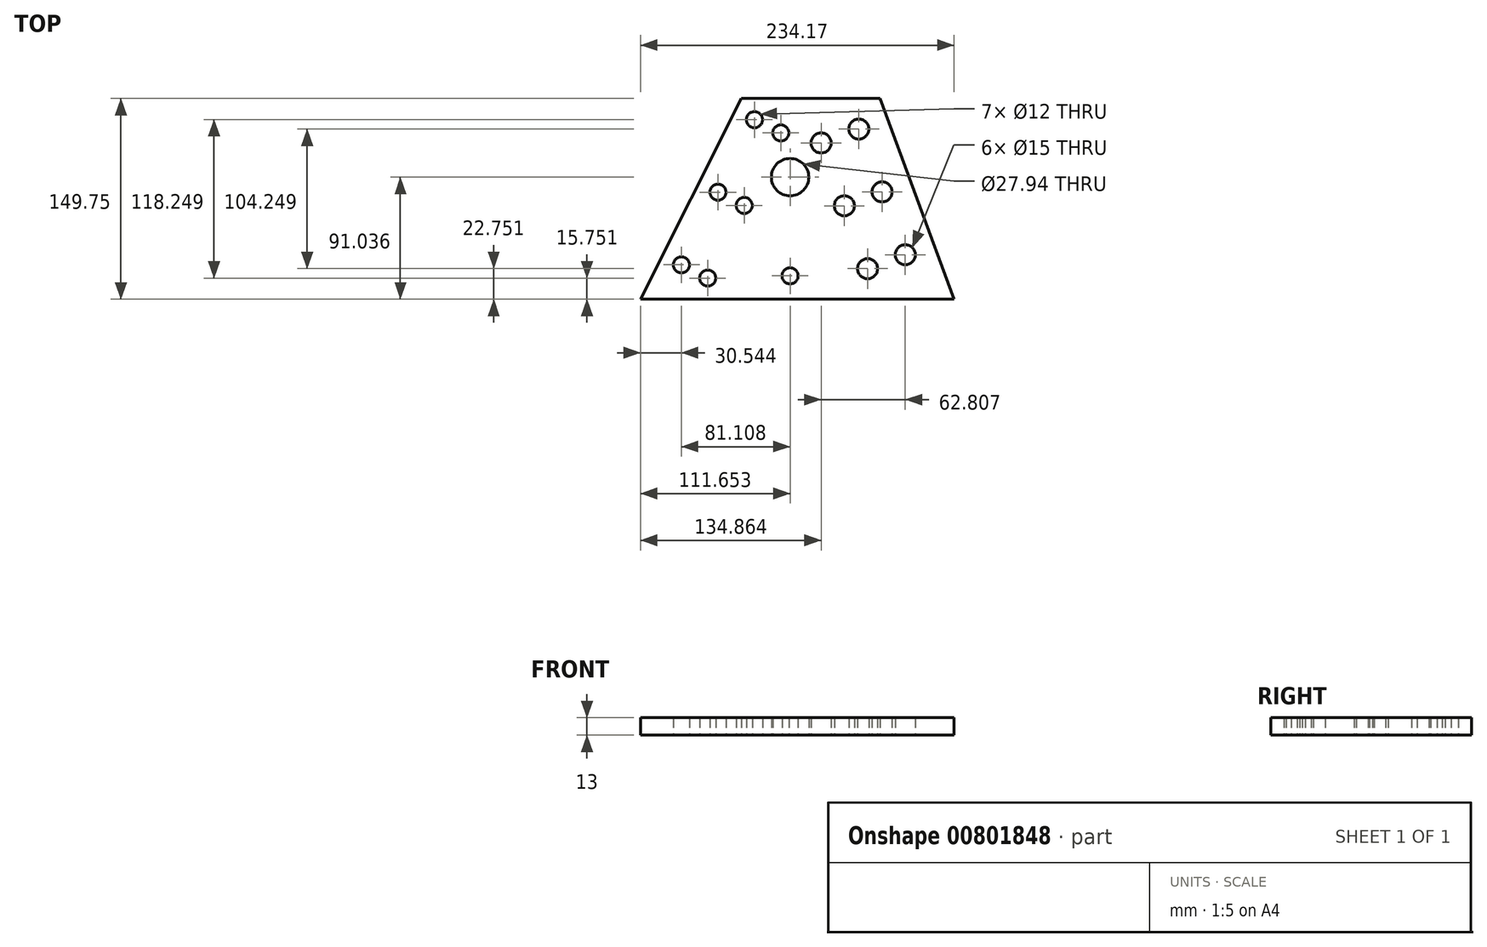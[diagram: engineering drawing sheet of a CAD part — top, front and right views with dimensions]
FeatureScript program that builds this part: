
annotation { "Feature Type Name" : "Feature", "Feature Type Description" : "" }
export const myFeature = defineFeature(function(context is Context, id is Id, definition is map)
    precondition{}
    {
        {
            var Q0;
            Q0=qCreatedBy(makeId("Top.planeOp"),FACE);
            var sketch = newSketch(context, id + "F0", { "sketchPlane" : qUnion([Q0])});
            skLineSegment(sketch, "E0", {"start": v(0, 0) * mm, "end": v(-107.38, -213.25) * mm, "construction": true});
            skLineSegment(sketch, "E1", {"start": v(-107.38, -213.25) * mm, "end": v(78.76, -213.25) * mm, "construction": true});
            skLineSegment(sketch, "E2", {"start": v(78.76, -213.25) * mm, "end": v(0, 0) * mm, "construction": true});
            skLineSegment(sketch, "E3", {"start": v(-124.54, -187.85) * mm, "end": v(109.63, -187.85) * mm});
            skLineSegment(sketch, "E4", {"start": v(-49.14, -38.1) * mm, "end": v(54.32, -38.1) * mm});
            skLineSegment(sketch, "E5", {"start": v(-49.14, -38.1) * mm, "end": v(-124.54, -187.85) * mm});
            skLineSegment(sketch, "E6", {"start": v(54.32, -38.1) * mm, "end": v(109.63, -187.85) * mm});
            skLineSegment(sketch, "E7", {"start": v(-19.78, -63.74) * mm, "end": v(-74.35, -172.1) * mm, "construction": true});
            skLineSegment(sketch, "E8", {"start": v(-94, -162.2) * mm, "end": v(-39.43, -53.85) * mm, "construction": true});
            skLineSegment(sketch, "E9", {"start": v(-19.78, -63.74) * mm, "end": v(-29.6, -58.8) * mm, "construction": true});
            skLineSegment(sketch, "E10", {"start": v(-39.43, -53.85) * mm, "end": v(-29.6, -58.8) * mm, "construction": true});
            skLineSegment(sketch, "E11", {"start": v(-74.35, -172.1) * mm, "end": v(-94, -162.2) * mm, "construction": true});
            skPoint(sketch, "E12", {"position": v(-66.71, -108.03) * mm});
            skPoint(sketch, "E13", {"position": v(-47.06, -117.92) * mm});
            skCircle(sketch, "E14", {"center": v(-39.43, -53.85) * mm, "radius": 2.25 * mm});
            skCircle(sketch, "E15", {"center": v(-19.78, -63.74) * mm, "radius": 2.25 * mm});
            skCircle(sketch, "E16", {"center": v(-47.06, -117.92) * mm, "radius": 2.25 * mm});
            skCircle(sketch, "E17", {"center": v(-66.71, -108.03) * mm, "radius": 2.25 * mm});
            skCircle(sketch, "E18", {"center": v(-94, -162.2) * mm, "radius": 2.25 * mm});
            skCircle(sketch, "E19", {"center": v(-74.35, -172.1) * mm, "radius": 2.25 * mm});
            skLineSegment(sketch, "E20", {"start": v(10.32, -71.24) * mm, "end": v(44.99, -165.1) * mm, "construction": true});
            skLineSegment(sketch, "E21", {"start": v(44.99, -165.1) * mm, "end": v(73.13, -154.7) * mm, "construction": true});
            skLineSegment(sketch, "E22", {"start": v(73.13, -154.7) * mm, "end": v(38.47, -60.85) * mm, "construction": true});
            skPoint(sketch, "E23", {"position": v(59.06, -159.9) * mm});
            skLineSegment(sketch, "E24", {"start": v(38.47, -60.85) * mm, "end": v(10.32, -71.24) * mm, "construction": true});
            skPoint(sketch, "E25", {"position": v(27.66, -118.17) * mm});
            skPoint(sketch, "E26", {"position": v(55.8, -107.78) * mm});
            skCircle(sketch, "E27", {"center": v(10.32, -71.24) * mm, "radius": 3.25 * mm});
            skCircle(sketch, "E28", {"center": v(27.66, -118.17) * mm, "radius": 3.25 * mm});
            skCircle(sketch, "E29", {"center": v(44.99, -165.1) * mm, "radius": 3.25 * mm});
            skCircle(sketch, "E30", {"center": v(73.13, -154.7) * mm, "radius": 3.25 * mm});
            skCircle(sketch, "E31", {"center": v(55.8, -107.78) * mm, "radius": 3.25 * mm});
            skCircle(sketch, "E32", {"center": v(38.47, -60.85) * mm, "radius": 3.25 * mm});
            skLineSegment(sketch, "E33.0", {"start": v(-40.53, -47.14) * mm, "end": v(-13.74, -60.63) * mm, "construction": true});
            skLineSegment(sketch, "E34.0", {"start": v(-40.53, -47.14) * mm, "end": v(-45.48, -56.96) * mm, "construction": true});
            skLineSegment(sketch, "E35.0", {"start": v(-13.74, -60.63) * mm, "end": v(-18.68, -70.46) * mm, "construction": true});
            skLineSegment(sketch, "E36.0", {"start": v(-45.48, -56.96) * mm, "end": v(-18.68, -70.46) * mm, "construction": true});
            skLineSegment(sketch, "E37.0", {"start": v(40.56, -52.08) * mm, "end": v(3.04, -65.94) * mm, "construction": true});
            skLineSegment(sketch, "E38.0", {"start": v(45.75, -66.15) * mm, "end": v(8.23, -80.01) * mm, "construction": true});
            skLineSegment(sketch, "E39.0", {"start": v(45.75, -66.15) * mm, "end": v(40.56, -52.08) * mm, "construction": true});
            skLineSegment(sketch, "E40.0", {"start": v(8.23, -80.01) * mm, "end": v(3.04, -65.94) * mm, "construction": true});
            skCircle(sketch, "E41", {"center": v(-12.89, -96.81) * mm, "radius": 13.34 * mm});
            skCircle(sketch, "E42", {"center": v(-12.89, -96.81) * mm, "radius": 26.99 * mm, "construction": true});
            skCircle(sketch, "E43", {"center": v(-12.89, -96.81) * mm, "radius": 102.23 * mm, "construction": true});
            skCircle(sketch, "E44", {"center": v(-12.89, -170.41) * mm, "radius": 3.24 * mm});
            skPoint(sketch, "E45", {"position": v(-12.89, -167.17) * mm});
            skPoint(sketch, "E46", {"position": v(-12.89, -173.65) * mm});
            skSolve(sketch);
        }
        {
            var Q0;
            Q0=qCreatedBy(makeId("Top.planeOp"),FACE);
            var sketch = newSketch(context, id + "F1", { "sketchPlane" : qUnion([Q0])});
            skPoint(sketch, "E47.0", {"position": v(-12.89, -96.81) * mm});
            skPoint(sketch, "E48.0", {"position": v(-12.89, -170.41) * mm});
            skCircle(sketch, "E49.0", {"center": v(-12.89, -96.81) * mm, "radius": 13.34 * mm});
            skCircle(sketch, "E50.0", {"center": v(-12.89, -170.41) * mm, "radius": 3.24 * mm});
            skLineSegment(sketch, "E51", {"start": v(12.51, -96.81) * mm, "end": v(12.51, -170.41) * mm});
            skLineSegment(sketch, "E52", {"start": v(-38.29, -96.81) * mm, "end": v(-38.29, -170.41) * mm});
            skArc(sketch, "E53", {"start": v(12.51, -96.81) * mm, "mid": v(-12.89, -71.41) * mm, "end": v(-38.29, -96.81) * mm});
            skArc(sketch, "E54", {"start": v(-38.29, -170.41) * mm, "mid": v(-12.89, -195.81) * mm, "end": v(12.51, -170.41) * mm});
            skSolve(sketch);
        }
        {
            var Q0;
            Q0=qCreatedBy(makeId("Top.planeOp"),FACE);
            var sketch = newSketch(context, id + "F2", { "sketchPlane" : qUnion([Q0])});
            skPoint(sketch, "E55.0", {"position": v(-49.14, -38.1) * mm});
            skPoint(sketch, "E56.0", {"position": v(54.32, -38.1) * mm});
            skPoint(sketch, "E57.0", {"position": v(109.63, -187.85) * mm});
            skPoint(sketch, "E58.0", {"position": v(-124.54, -187.85) * mm});
            skPoint(sketch, "E59.0", {"position": v(-94, -162.2) * mm});
            skPoint(sketch, "E60.0", {"position": v(-74.35, -172.1) * mm});
            skPoint(sketch, "E61.0", {"position": v(-47.06, -117.92) * mm});
            skPoint(sketch, "E62.0", {"position": v(-66.71, -108.03) * mm});
            skPoint(sketch, "E63.0", {"position": v(-39.43, -53.85) * mm});
            skPoint(sketch, "E64.0", {"position": v(-19.78, -63.74) * mm});
            skPoint(sketch, "E65.0", {"position": v(10.32, -71.24) * mm});
            skPoint(sketch, "E66.0", {"position": v(27.66, -118.17) * mm});
            skPoint(sketch, "E67.0", {"position": v(44.99, -165.1) * mm});
            skPoint(sketch, "E68.0", {"position": v(73.13, -154.7) * mm});
            skPoint(sketch, "E69.0", {"position": v(55.8, -107.78) * mm});
            skPoint(sketch, "E70.0", {"position": v(38.47, -60.85) * mm});
            skPoint(sketch, "E71.0", {"position": v(-12.89, -96.81) * mm});
            skPoint(sketch, "E72.0", {"position": v(-12.89, -170.41) * mm});
            skLineSegment(sketch, "E73", {"start": v(-49.14, -38.1) * mm, "end": v(54.32, -38.1) * mm});
            skLineSegment(sketch, "E74", {"start": v(109.63, -187.85) * mm, "end": v(54.32, -38.1) * mm});
            skLineSegment(sketch, "E75", {"start": v(-124.54, -187.85) * mm, "end": v(109.63, -187.85) * mm});
            skLineSegment(sketch, "E76", {"start": v(-124.54, -187.85) * mm, "end": v(-49.14, -38.1) * mm});
            skSolve(sketch);
        }
        {
            var Q0;
            Q0=makeQuery(id+"F2.imprint","IMPRINT",FACE,{"disambiguationData":[TD([[makeQuery(id+"F2.imprint","IMPRINT",EDGE,{"derivedFrom":sQuery(id+"F2.wireOp",EDGE,"E73")}),-1.0]])]});
            extrude(context, id + "F3", {"entities" : qUnion([Q0]), "depth" : 13 * mm, "offsetDistance" : 25.4 * mm});
        }
        {
            var Q0;
            Q0=sQuery(id+"F2.wireOp",VERTEX,"E70.0");
            var Q1;
            Q1=sQuery(id+"F2.wireOp",VERTEX,"E65.0");
            var Q2;
            Q2=sQuery(id+"F2.wireOp",VERTEX,"E66.0");
            var Q3;
            Q3=sQuery(id+"F2.wireOp",VERTEX,"E69.0");
            var Q4;
            Q4=sQuery(id+"F2.wireOp",VERTEX,"E67.0");
            var Q5;
            Q5=sQuery(id+"F2.wireOp",VERTEX,"E68.0");
            var Q6;
            Q6=makeQuery(id+"F3.opExtrude","SWEPT_BODY",BODY,{"disambiguationData":[OSD([sQuery(id+"F2.wireOp",EDGE,"E73"),sQuery(id+"F2.wireOp",EDGE,"E74"),sQuery(id+"F2.wireOp",EDGE,"E75"),sQuery(id+"F2.wireOp",EDGE,"E76")])]});
            hole(context, id + "F4", {"style" : HoleStyle.SIMPLE, "endStyle" : HoleEndStyle.THROUGH, "oppositeDirection" : true, "holeDiameter" : 15 * mm, "majorDiameter" : 6.35 * mm, "isTappedThrough" : true, "tappedDepth" : 12 * mm, "tapClearance" : 3, "startFromSketch" : true, "locations" : qUnion([Q0, Q1, Q2, Q3, Q4, Q5]), "scope" : qUnion([Q6])});
        }
        {
            var Q0;
            Q0=sQuery(id+"F2.wireOp",VERTEX,"E64.0");
            var Q1;
            Q1=sQuery(id+"F2.wireOp",VERTEX,"E63.0");
            var Q2;
            Q2=sQuery(id+"F2.wireOp",VERTEX,"E62.0");
            var Q3;
            Q3=sQuery(id+"F2.wireOp",VERTEX,"E61.0");
            var Q4;
            Q4=sQuery(id+"F2.wireOp",VERTEX,"E60.0");
            var Q5;
            Q5=sQuery(id+"F2.wireOp",VERTEX,"E59.0");
            var Q6;
            Q6=sQuery(id+"F2.wireOp",VERTEX,"E72.0");
            var Q7;
            Q7=makeQuery(id+"F3.opExtrude","SWEPT_BODY",BODY,{"disambiguationData":[OSD([sQuery(id+"F2.wireOp",EDGE,"E73"),sQuery(id+"F2.wireOp",EDGE,"E74"),sQuery(id+"F2.wireOp",EDGE,"E75"),sQuery(id+"F2.wireOp",EDGE,"E76")])]});
            hole(context, id + "F5", {"style" : HoleStyle.SIMPLE, "endStyle" : HoleEndStyle.THROUGH, "oppositeDirection" : true, "holeDiameter" : 12 * mm, "majorDiameter" : 6.35 * mm, "isTappedThrough" : true, "tappedDepth" : 12 * mm, "tapClearance" : 3, "startFromSketch" : true, "locations" : qUnion([Q0, Q1, Q2, Q3, Q4, Q5, Q6]), "scope" : qUnion([Q7])});
        }
        {
            var Q0;
            Q0=sQuery(id+"F2.wireOp",VERTEX,"E71.0");
            var Q1;
            Q1=makeQuery(id+"F3.opExtrude","SWEPT_BODY",BODY,{"disambiguationData":[OSD([sQuery(id+"F2.wireOp",EDGE,"E73"),sQuery(id+"F2.wireOp",EDGE,"E74"),sQuery(id+"F2.wireOp",EDGE,"E75"),sQuery(id+"F2.wireOp",EDGE,"E76")])]});
            hole(context, id + "F6", {"style" : HoleStyle.SIMPLE, "endStyle" : HoleEndStyle.THROUGH, "oppositeDirection" : true, "holeDiameter" : 27.94 * mm, "majorDiameter" : 6.35 * mm, "isTappedThrough" : true, "tappedDepth" : 12 * mm, "tapClearance" : 3, "startFromSketch" : true, "locations" : qUnion([Q0]), "scope" : qUnion([Q1])});
        }
    });
